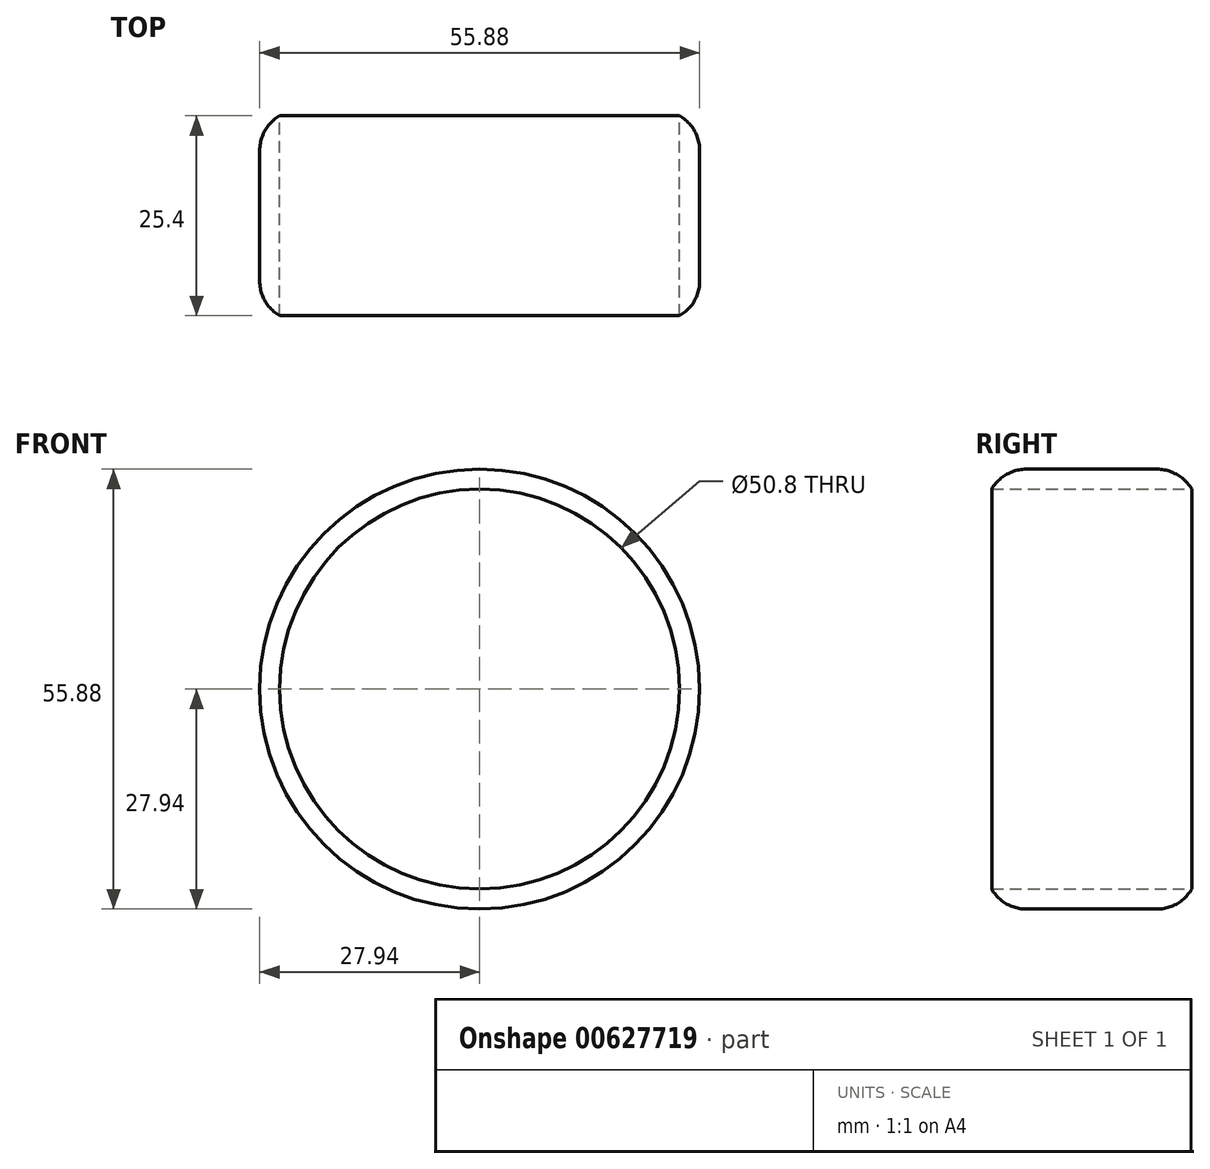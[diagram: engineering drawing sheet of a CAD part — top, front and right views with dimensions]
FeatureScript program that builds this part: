
annotation { "Feature Type Name" : "Feature", "Feature Type Description" : "" }
export const myFeature = defineFeature(function(context is Context, id is Id, definition is map)
    precondition{}
    {
        {
            var Q0;
            Q0=qCreatedBy(makeId("Front.planeOp"),FACE);
            var sketch = newSketch(context, id + "F0", { "sketchPlane" : qUnion([Q0])});
            skCircle(sketch, "E0", {"center": v(0, 0) * mm, "radius": 27.94 * mm});
            skCircle(sketch, "E1", {"center": v(0, 0) * mm, "radius": 25.4 * mm});
            skSolve(sketch);
        }
        {
            var Q0;
            Q0=qSketchRegion(id+"F0",true);
            extrude(context, id + "F1", {"entities" : qUnion([Q0]), "depth" : 25.4 * mm, "offsetDistance" : 25.4 * mm});
        }
        {
            var Q0;
            Q0=makeQuery(id+"F1.opExtrude","CAP_EDGE",EDGE,{"disambiguationData":[OSD([sQuery(id+"F0.wireOp",EDGE,"E0")])],"isStart":true});
            var Q1;
            Q1=makeQuery(id+"F1.opExtrude","CAP_EDGE",EDGE,{"disambiguationData":[OSD([sQuery(id+"F0.wireOp",EDGE,"E0")])],"isStart":false});
            fillet(context, id + "F2", {"entities" : qUnion([Q0, Q1]), "radius" : 5.08 * mm, "tangentPropagation" : true, "allowEdgeOverflow" : false});
        }
    });
